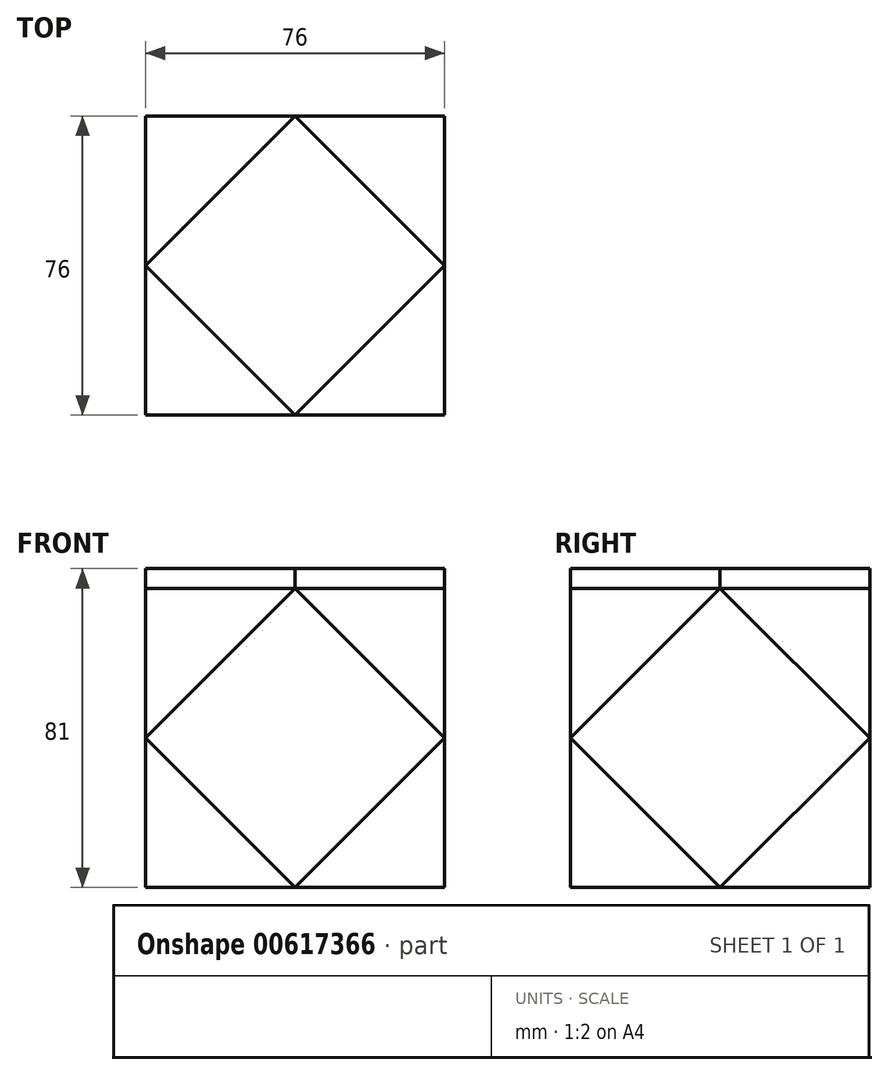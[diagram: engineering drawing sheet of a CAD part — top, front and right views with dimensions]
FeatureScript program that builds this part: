
annotation { "Feature Type Name" : "Feature", "Feature Type Description" : "" }
export const myFeature = defineFeature(function(context is Context, id is Id, definition is map)
    precondition{}
    {
        {
            var Q0;
            Q0=qCreatedBy(makeId("Top.planeOp"),FACE);
            var sketch = newSketch(context, id + "F0", { "sketchPlane" : qUnion([Q0])});
            skLineSegment(sketch, "E0.bottom", {"start": v(0, 0) * mm, "end": v(-38, 0) * mm});
            skLineSegment(sketch, "E0.top", {"start": v(0, 38) * mm, "end": v(-38, 38) * mm});
            skLineSegment(sketch, "E0.left", {"start": v(0, 0) * mm, "end": v(0, 38) * mm});
            skLineSegment(sketch, "E0.right", {"start": v(-38, 0) * mm, "end": v(-38, 38) * mm});
            skSolve(sketch);
        }
        {
            var Q0;
            Q0=makeQuery(id+"F0.imprint","IMPRINT",FACE,{"disambiguationData":[TD([[makeQuery(id+"F0.imprint","IMPRINT",EDGE,{"derivedFrom":sQuery(id+"F0.wireOp",EDGE,"E0.bottom")}),-1.0]])]});
            extrude(context, id + "F1", {"entities" : qUnion([Q0]), "depth" : 76 * mm, "offsetDistance" : 25 * mm});
        }
        {
            var Q0;
            Q0=qCreatedBy(makeId("Top.planeOp"),FACE);
            var sketch = newSketch(context, id + "F2", { "sketchPlane" : qUnion([Q0])});
            skLineSegment(sketch, "E1", {"start": v(-76, -38) * mm, "end": v(0, 38) * mm});
            skSolve(sketch);
        }
        {
            var Q0;
            Q0=makeQuery(id+"F1.opExtrude","SWEPT_FACE",FACE,{"disambiguationData":[OSD([sQuery(id+"F0.wireOp",EDGE,"E0.right")])]});
            var sketch = newSketch(context, id + "F3", { "sketchPlane" : qUnion([Q0])});
            skLineSegment(sketch, "E2", {"start": v(0, 0) * mm, "end": v(-38, 0) * mm});
            skLineSegment(sketch, "E3", {"start": v(-38, 0) * mm, "end": v(-38, 76) * mm});
            skLineSegment(sketch, "E4", {"start": v(-38, 76) * mm, "end": v(0, 76) * mm});
            skLineSegment(sketch, "E5", {"start": v(0, 76) * mm, "end": v(-38, 38) * mm});
            skLineSegment(sketch, "E6", {"start": v(-38, 38) * mm, "end": v(0, 0) * mm});
            skSolve(sketch);
        }
        {
            var Q0;
            Q0 = qSketchRegion(id + "F3", true);
            var Q1;
            Q1=sQuery(id+"F2.wireOp",EDGE,"E1");
            sweep(context, id + "F4", {"operationType" : NewBodyOperationType.REMOVE, "profiles" : qUnion([Q0]), "path" : qUnion([Q1])});
        }
        {
            var Q0;
            Q0=makeQuery(id+"F1.opExtrude","SWEPT_BODY",BODY,{"disambiguationData":[OSD([sQuery(id+"F0.wireOp",EDGE,"E0.bottom"),sQuery(id+"F0.wireOp",EDGE,"E0.top"),sQuery(id+"F0.wireOp",EDGE,"E0.left"),sQuery(id+"F0.wireOp",EDGE,"E0.right")])]});
            var Q1;
            Q1=makeQuery(id+"F1.opExtrude","SWEPT_EDGE",EDGE,{"disambiguationData":[OSD([sQuery(id+"F0.wireOp",EDGE,"E0.bottom"),sQuery(id+"F0.wireOp",EDGE,"E0.left")])]});
            circularPattern(context, id + "F5", {"entities" : qUnion([Q0]), "axis" : qUnion([Q1]), "angle" : 360 * degree, "instanceCount" : 4, "equalSpace" : true});
        }
        {
            var Q0;
            Q0=makeQuery(id+"F5.opPattern","COPY",BODY,{"derivedFrom":makeQuery(id+"F1.opExtrude","SWEPT_BODY",BODY,{"disambiguationData":[OSD([sQuery(id+"F0.wireOp",EDGE,"E0.bottom"),sQuery(id+"F0.wireOp",EDGE,"E0.top"),sQuery(id+"F0.wireOp",EDGE,"E0.left"),sQuery(id+"F0.wireOp",EDGE,"E0.right")])]}),"instanceName":"1"});
            var Q1;
            Q1=makeQuery(id+"F1.opExtrude","SWEPT_BODY",BODY,{"disambiguationData":[OSD([sQuery(id+"F0.wireOp",EDGE,"E0.bottom"),sQuery(id+"F0.wireOp",EDGE,"E0.top"),sQuery(id+"F0.wireOp",EDGE,"E0.left"),sQuery(id+"F0.wireOp",EDGE,"E0.right")])]});
            var Q2;
            Q2=makeQuery(id+"F5.opPattern","COPY",BODY,{"derivedFrom":makeQuery(id+"F1.opExtrude","SWEPT_BODY",BODY,{"disambiguationData":[OSD([sQuery(id+"F0.wireOp",EDGE,"E0.bottom"),sQuery(id+"F0.wireOp",EDGE,"E0.top"),sQuery(id+"F0.wireOp",EDGE,"E0.left"),sQuery(id+"F0.wireOp",EDGE,"E0.right")])]}),"instanceName":"3"});
            var Q3;
            Q3=makeQuery(id+"F5.opPattern","COPY",BODY,{"derivedFrom":makeQuery(id+"F1.opExtrude","SWEPT_BODY",BODY,{"disambiguationData":[OSD([sQuery(id+"F0.wireOp",EDGE,"E0.bottom"),sQuery(id+"F0.wireOp",EDGE,"E0.top"),sQuery(id+"F0.wireOp",EDGE,"E0.left"),sQuery(id+"F0.wireOp",EDGE,"E0.right")])]}),"instanceName":"2"});
            booleanBodies(context, id + "F6", {"operationType" : BooleanOperationType.UNION, "tools" : qUnion([Q0, Q1, Q2, Q3])});
        }
        {
            var Q0;
            {var subQ0=makeQuery(id+"F1.opExtrude","CAP_FACE",FACE,{"disambiguationData":[OSD([sQuery(id+"F0.wireOp",EDGE,"E0.bottom"),sQuery(id+"F0.wireOp",EDGE,"E0.top"),sQuery(id+"F0.wireOp",EDGE,"E0.left"),sQuery(id+"F0.wireOp",EDGE,"E0.right")])],"isStart":false});Q0=makeQuery(id+"F6.opBoolean","MERGE",FACE,{"derivedFrom":[subQ0,makeQuery(id+"F5.opPattern","COPY",FACE,{"derivedFrom":subQ0,"instanceName":"1"}),makeQuery(id+"F5.opPattern","COPY",FACE,{"derivedFrom":subQ0,"instanceName":"2"}),makeQuery(id+"F5.opPattern","COPY",FACE,{"derivedFrom":subQ0,"instanceName":"3"})]});}
            var sketch = newSketch(context, id + "F7", { "sketchPlane" : qUnion([Q0])});
            skLineSegment(sketch, "E7", {"start": v(0, -38) * mm, "end": v(38, 0) * mm});
            skLineSegment(sketch, "E8", {"start": v(38, 0) * mm, "end": v(0, 38) * mm});
            skLineSegment(sketch, "E9", {"start": v(0, 38) * mm, "end": v(-38, 0) * mm});
            skLineSegment(sketch, "E10", {"start": v(-38, 0) * mm, "end": v(0, -38) * mm});
            skSolve(sketch);
        }
        {
            var Q0;
            Q0 = qSketchRegion(id + "F7", true);
            extrude(context, id + "F8", {"entities" : qUnion([Q0]), "operationType" : NewBodyOperationType.ADD, "depth" : 5 * mm, "offsetDistance" : 25 * mm});
        }
    });
